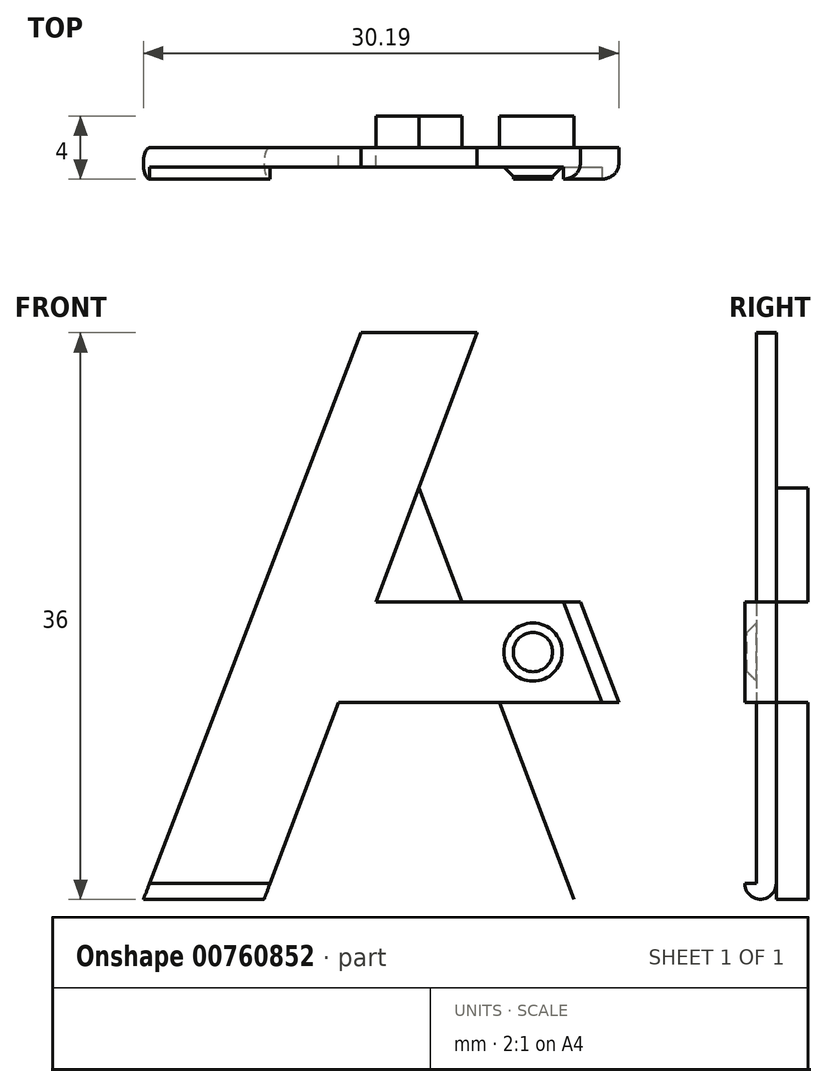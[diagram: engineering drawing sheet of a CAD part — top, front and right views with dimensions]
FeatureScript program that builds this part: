
annotation { "Feature Type Name" : "Feature", "Feature Type Description" : "" }
export const myFeature = defineFeature(function(context is Context, id is Id, definition is map)
    precondition{}
    {
        {
            var Q0;
            Q0=qCreatedBy(makeId("Front.planeOp"),FACE);
            var sketch = newSketch(context, id + "F0", { "sketchPlane" : qUnion([Q0])});
            skLineSegment(sketch, "E0", {"start": v(3.69, 18) * mm, "end": v(17.5, -18) * mm});
            skLineSegment(sketch, "E1", {"start": v(17.5, -18) * mm, "end": v(9.84, -18) * mm});
            skLineSegment(sketch, "E2", {"start": v(9.84, -18) * mm, "end": v(-3.7, 18) * mm});
            skLineSegment(sketch, "E3", {"start": v(-3.7, 18) * mm, "end": v(3.69, 18) * mm});
            skLineSegment(sketch, "E4", {"start": v(12.78, -5.47) * mm, "end": v(10.39, 0.9) * mm});
            skLineSegment(sketch, "E5", {"start": v(10.39, 0.9) * mm, "end": v(-2.73, 0.9) * mm});
            skLineSegment(sketch, "E6", {"start": v(-2.73, 0.9) * mm, "end": v(3.7, 18) * mm});
            skLineSegment(sketch, "E7", {"start": v(3.7, 18) * mm, "end": v(-3.69, 18) * mm});
            skLineSegment(sketch, "E8", {"start": v(-3.69, 18) * mm, "end": v(-17.5, -18) * mm});
            skLineSegment(sketch, "E9", {"start": v(-17.5, -18) * mm, "end": v(-9.84, -18) * mm});
            skLineSegment(sketch, "E10", {"start": v(-9.84, -18) * mm, "end": v(-5.13, -5.47) * mm});
            skLineSegment(sketch, "E11", {"start": v(-5.13, -5.47) * mm, "end": v(12.78, -5.47) * mm});
            skSolve(sketch);
        }
        {
            var Q0;
            {var subQ10=sQuery(id+"F0.wireOp",EDGE,"E9");Q0=makeQuery(id+"F0.imprint","IMPRINT",FACE,{"disambiguationData":[TD([[makeQuery(id+"F0.imprint","IMPRINT",EDGE,{"derivedFrom":subQ10}),1.0]])]});}
            var Q1;
            {var subQ0=sQuery(id+"F0.wireOp",EDGE,"E7");var subQ1=sQuery(id+"F0.wireOp",EDGE,"E0");var subQ2=makeQuery(id+"F0.imprint","INTERSECT",VERTEX,{"derivedFrom":[subQ1,subQ0]});Q1=makeQuery(id+"F0.imprint","IMPRINT",FACE,{"disambiguationData":[TD([[makeQuery(id+"F0.imprint","IMPRINT",EDGE,{"disambiguationData":[TD([[subQ2,-1.0]])],"derivedFrom":subQ1}),-1.0]])]});}
            var Q2;
            {var subQ0=sQuery(id+"F0.wireOp",EDGE,"E5");var subQ1=sQuery(id+"F0.wireOp",EDGE,"E0");var subQ2=makeQuery(id+"F0.imprint","INTERSECT",VERTEX,{"derivedFrom":[subQ1,subQ0]});Q2=makeQuery(id+"F0.imprint","IMPRINT",FACE,{"disambiguationData":[TD([[makeQuery(id+"F0.imprint","IMPRINT",EDGE,{"disambiguationData":[TD([[subQ2,-1.0]])],"derivedFrom":subQ1}),-1.0]])]});}
            extrude(context, id + "F1", {"entities" : qUnion([Q0, Q1, Q2]), "depth" : 2 * mm, "offsetDistance" : 25 * mm});
        }
        {
            var Q0;
            Q0=qCreatedBy(makeId("Front.planeOp"),FACE);
            var sketch = newSketch(context, id + "F2", { "sketchPlane" : qUnion([Q0])});
            skLineSegment(sketch, "E12", {"start": v(3.69, 18) * mm, "end": v(17.5, -18) * mm});
            skLineSegment(sketch, "E13", {"start": v(17.5, -18) * mm, "end": v(9.84, -18) * mm});
            skLineSegment(sketch, "E14", {"start": v(9.84, -18) * mm, "end": v(-3.7, 18) * mm});
            skLineSegment(sketch, "E15", {"start": v(-3.7, 18) * mm, "end": v(3.69, 18) * mm});
            skLineSegment(sketch, "E16", {"start": v(12.78, -5.47) * mm, "end": v(10.39, 0.9) * mm});
            skLineSegment(sketch, "E17", {"start": v(10.39, 0.9) * mm, "end": v(-2.73, 0.9) * mm});
            skLineSegment(sketch, "E18", {"start": v(-2.73, 0.9) * mm, "end": v(3.7, 18) * mm});
            skLineSegment(sketch, "E19", {"start": v(3.7, 18) * mm, "end": v(-3.69, 18) * mm});
            skLineSegment(sketch, "E20", {"start": v(-3.69, 18) * mm, "end": v(-17.5, -18) * mm});
            skLineSegment(sketch, "E21", {"start": v(-17.5, -18) * mm, "end": v(-9.84, -18) * mm});
            skLineSegment(sketch, "E22", {"start": v(-9.84, -18) * mm, "end": v(-5.13, -5.47) * mm});
            skLineSegment(sketch, "E23", {"start": v(-5.13, -5.47) * mm, "end": v(12.78, -5.47) * mm});
            skLineSegment(sketch, "E24", {"start": v(-9.84, -18) * mm, "end": v(3.7, 18) * mm});
            skLineSegment(sketch, "E25", {"start": v(-12.7, -5.47) * mm, "end": v(-10.25, 0.9) * mm});
            skLineSegment(sketch, "E26", {"start": v(-10.25, 0.9) * mm, "end": v(2.73, 0.9) * mm});
            skLineSegment(sketch, "E27", {"start": v(2.73, 0.9) * mm, "end": v(-3.7, 18) * mm});
            skLineSegment(sketch, "E28", {"start": v(9.84, -18) * mm, "end": v(5.13, -5.47) * mm});
            skLineSegment(sketch, "E29", {"start": v(5.13, -5.47) * mm, "end": v(-12.7, -5.47) * mm});
            skSolve(sketch);
        }
        {
            var Q0;
            {var subQ1=sQuery(id+"F2.wireOp",EDGE,"E17");var subQ3=sQuery(id+"F2.wireOp",EDGE,"E12");var subQ4=makeQuery(id+"F2.imprint","INTERSECT",VERTEX,{"derivedFrom":[subQ1,subQ3]});Q0=makeQuery(id+"F2.imprint","IMPRINT",FACE,{"disambiguationData":[TD([[makeQuery(id+"F2.imprint","IMPRINT",EDGE,{"disambiguationData":[TD([[subQ4,1.0]])],"derivedFrom":subQ3}),-1.0]])]});}
            var Q1;
            {var subQ3=sQuery(id+"F2.wireOp",EDGE,"E20");var subQ5=sQuery(id+"F2.wireOp",EDGE,"E15");var subQ6=makeQuery(id+"F2.imprint","INTERSECT",VERTEX,{"derivedFrom":[subQ3,subQ5]});Q1=makeQuery(id+"F2.imprint","IMPRINT",FACE,{"disambiguationData":[TD([[makeQuery(id+"F2.imprint","IMPRINT",EDGE,{"disambiguationData":[TD([[subQ6,-1.0]])],"derivedFrom":subQ3}),1.0]])]});}
            var Q2;
            {var subQ0=sQuery(id+"F2.wireOp",EDGE,"E14");Q2=makeQuery(id+"F2.imprint","IMPRINT",FACE,{"disambiguationData":[TD([[makeQuery(id+"F2.imprint","IMPRINT",EDGE,{"derivedFrom":subQ0}),-1.0]])]});}
            var Q3;
            {var subQ0=sQuery(id+"F2.wireOp",EDGE,"E14");Q3=makeQuery(id+"F2.imprint","IMPRINT",FACE,{"disambiguationData":[TD([[makeQuery(id+"F2.imprint","IMPRINT",EDGE,{"derivedFrom":subQ0}),1.0]])]});}
            var Q4;
            {var subQ5=sQuery(id+"F2.wireOp",EDGE,"E25");Q4=makeQuery(id+"F2.imprint","IMPRINT",FACE,{"disambiguationData":[TD([[makeQuery(id+"F2.imprint","IMPRINT",EDGE,{"derivedFrom":subQ5}),-1.0]])]});}
            var Q5;
            {var subQ4=sQuery(id+"F2.wireOp",EDGE,"E13");Q5=makeQuery(id+"F2.imprint","IMPRINT",FACE,{"disambiguationData":[TD([[makeQuery(id+"F2.imprint","IMPRINT",EDGE,{"derivedFrom":subQ4}),-1.0]])]});}
            extrude(context, id + "F3", {"entities" : qUnion([Q0, Q1, Q2, Q3, Q4, Q5]), "operationType" : NewBodyOperationType.ADD, "oppositeDirection" : true, "depth" : 2 * mm, "offsetDistance" : 25 * mm});
        }
        {
            var Q0;
            Q0=makeQuery(id+"F3.opExtrude","CAP_FACE",FACE,{"disambiguationData":[OSD([sQuery(id+"F2.wireOp",EDGE,"E20"),sQuery(id+"F2.wireOp",EDGE,"E25"),sQuery(id+"F2.wireOp",EDGE,"E26"),sQuery(id+"F2.wireOp",EDGE,"E27"),sQuery(id+"F2.wireOp",EDGE,"E15"),sQuery(id+"F2.wireOp",EDGE,"E12"),sQuery(id+"F2.wireOp",EDGE,"E13"),sQuery(id+"F2.wireOp",EDGE,"E28"),sQuery(id+"F2.wireOp",EDGE,"E29")])],"isStart":false});
            var sketch = newSketch(context, id + "F4", { "sketchPlane" : qUnion([Q0])});
            skText(sketch, "E30", { "text": "RISK POWERS PERFORMANCE", "fontName": "OpenSans-Regular.ttf"});
            skLineSegment(sketch, "E31.0", {"start": v(-11.95, -14.2) * mm, "end": v(-0.55, 13.55) * mm, "construction": true});
            skLineSegment(sketch, "E31.1", {"start": v(-11.95, -14.2) * mm, "end": v(-11.95, -14.2) * mm});
            skText(sketch, "E32", { "text": "2017", "fontName": "OpenSans-Regular.ttf"});
            const initialGuessF4  = {"E30": [-0.01194, -0.01418, 0.3638, 0.93148, 0.00157], "E32": [0.0028, -0.00302, 1, 0, 0.00182]};
            skSetInitialGuess(sketch, initialGuessF4);
            skSolve(sketch);
        }
        {
            var Q0;
            Q0 = qSketchRegion(id + "F4", true);
            extrude(context, id + "F5", {"entities" : qUnion([Q0]), "operationType" : NewBodyOperationType.REMOVE, "oppositeDirection" : true, "depth" : 0.5 * mm, "offsetDistance" : 25 * mm});
        }
        {
            var Q0;
            Q0=makeQuery(id+"F1.opExtrude","CAP_EDGE",EDGE,{"disambiguationData":[OSD([sQuery(id+"F0.wireOp",EDGE,"E7")])],"isStart":false});
            var Q1;
            Q1=makeQuery(id+"F3.opExtrude","CAP_EDGE",EDGE,{"disambiguationData":[OSD([sQuery(id+"F2.wireOp",EDGE,"E15")])],"isStart":false});
            var Q2;
            Q2=makeQuery(id+"F1.opExtrude","CAP_EDGE",EDGE,{"disambiguationData":[OSD([sQuery(id+"F0.wireOp",EDGE,"E9")])],"isStart":false});
            var Q3;
            Q3=makeQuery(id+"F3.opExtrude","CAP_EDGE",EDGE,{"disambiguationData":[OSD([sQuery(id+"F2.wireOp",EDGE,"E13")])],"isStart":true});
            var Q4;
            Q4=makeQuery(id+"F1.opExtrude","CAP_EDGE",EDGE,{"disambiguationData":[OSD([sQuery(id+"F0.wireOp",EDGE,"E9")])],"isStart":true});
            var Q5;
            Q5=makeQuery(id+"F3.opExtrude","CAP_EDGE",EDGE,{"disambiguationData":[OSD([sQuery(id+"F2.wireOp",EDGE,"E13")])],"isStart":false});
            var Q6;
            {var subQ0=sQuery(id+"F0.wireOp",EDGE,"E0");Q6=makeQuery(id+"F1.opExtrude","CAP_EDGE",EDGE,{"disambiguationData":[OSD([subQ0]),TDD([makeQuery(id+"F0.imprint","IMPRINT",EDGE,{"disambiguationData":[TD([[makeQuery(id+"F0.imprint","INTERSECT",VERTEX,{"derivedFrom":[subQ0,sQuery(id+"F0.wireOp",EDGE,"E5")]}),-1.0]])],"derivedFrom":subQ0})])],"isStart":false});}
            var Q7;
            Q7=makeQuery(id+"F3.opExtrude","CAP_EDGE",EDGE,{"disambiguationData":[OSD([sQuery(id+"F2.wireOp",EDGE,"E25")])],"isStart":false});
            fillet(context, id + "F6", {"entities" : qUnion([Q0, Q1, Q2, Q3, Q4, Q5, Q6, Q7]), "radius" : 1 * mm, "tangentPropagation" : true, "allowEdgeOverflow" : false});
        }
        {
            var Q0;
            Q0=makeQuery(id+"F1.opExtrude","CAP_FACE",FACE,{"disambiguationData":[OSD([sQuery(id+"F0.wireOp",EDGE,"E0"),sQuery(id+"F0.wireOp",EDGE,"E5"),sQuery(id+"F0.wireOp",EDGE,"E6"),sQuery(id+"F0.wireOp",EDGE,"E7"),sQuery(id+"F0.wireOp",EDGE,"E8"),sQuery(id+"F0.wireOp",EDGE,"E9"),sQuery(id+"F0.wireOp",EDGE,"E10"),sQuery(id+"F0.wireOp",EDGE,"E11")])],"isStart":false});
            var sketch = newSketch(context, id + "F7", { "sketchPlane" : qUnion([Q0])});
            skLineSegment(sketch, "E33", {"start": v(10.4, -2.3) * mm, "end": v(-11.47, -2.3) * mm});
            skCircle(sketch, "E34", {"center": v(7.24, -2.3) * mm, "radius": 1.25 * mm});
            skSolve(sketch);
        }
        {
            var Q0;
            {var subQ0=sQuery(id+"F7.wireOp",EDGE,"E34");var subQ1=sQuery(id+"F7.wireOp",EDGE,"E33");var subQ2=makeQuery(id+"F7.imprint","INTERSECT",VERTEX,{"disambiguationData":[OD(0.0)],"derivedFrom":[subQ1,subQ0]});Q0=makeQuery(id+"F7.imprint","IMPRINT",FACE,{"disambiguationData":[TD([[makeQuery(id+"F7.imprint","IMPRINT",EDGE,{"disambiguationData":[TD([[subQ2,-1.0]])],"derivedFrom":subQ1}),-1.0]])]});}
            var Q1;
            {var subQ0=sQuery(id+"F7.wireOp",EDGE,"E34");var subQ1=sQuery(id+"F7.wireOp",EDGE,"E33");var subQ2=makeQuery(id+"F7.imprint","INTERSECT",VERTEX,{"disambiguationData":[OD(0.0)],"derivedFrom":[subQ1,subQ0]});Q1=makeQuery(id+"F7.imprint","IMPRINT",FACE,{"disambiguationData":[TD([[makeQuery(id+"F7.imprint","IMPRINT",EDGE,{"disambiguationData":[TD([[subQ2,-1.0]])],"derivedFrom":subQ1}),1.0]])]});}
            extrude(context, id + "F8", {"entities" : qUnion([Q0, Q1]), "operationType" : NewBodyOperationType.REMOVE, "endBound" : BoundingType.SYMMETRIC, "oppositeDirection" : true, "depth" : 1.5 * mm, "offsetDistance" : 25 * mm});
        }
        {
            var Q0;
            Q0=makeQuery(id+"F8.boolean.opBoolean","COPY",EDGE,{"derivedFrom":makeQuery(id+"F8.opExtrude","CAP_EDGE",EDGE,{"disambiguationData":[OSD([sQuery(id+"F7.wireOp",EDGE,"E34")])],"isStart":false})});
            chamfer(context, id + "F9", {"entities" : qUnion([Q0]), "width" : 0.6 * mm});
        }
    });
